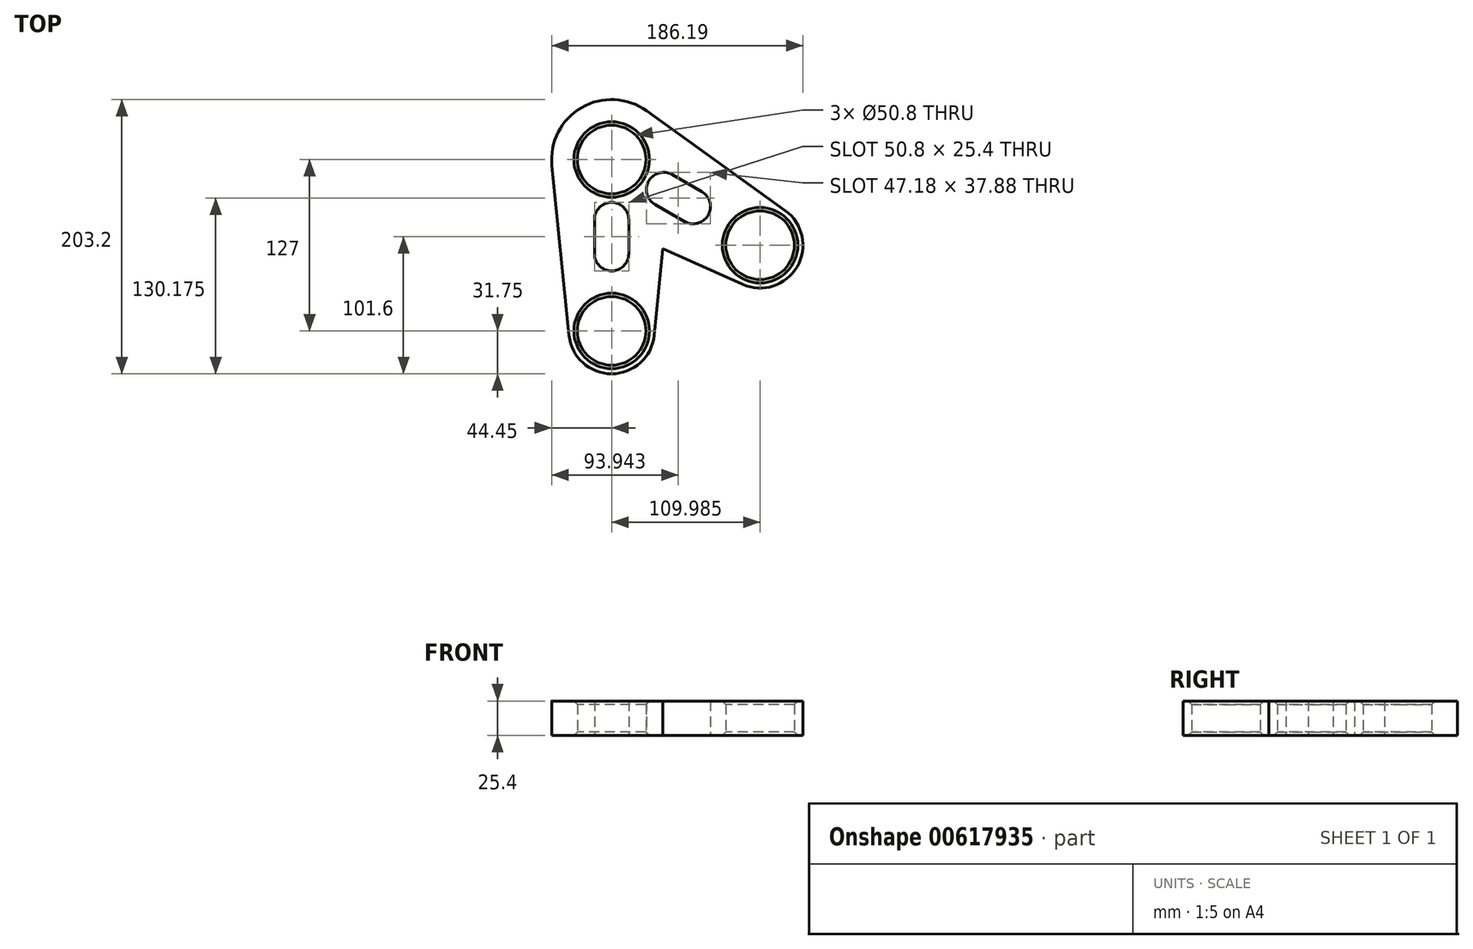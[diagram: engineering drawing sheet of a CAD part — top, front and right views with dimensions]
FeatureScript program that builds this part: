
annotation { "Feature Type Name" : "Feature", "Feature Type Description" : "" }
export const myFeature = defineFeature(function(context is Context, id is Id, definition is map)
    precondition{}
    {
        {
            var Q0;
            Q0=qCreatedBy(makeId("Top.planeOp"),FACE);
            var sketch = newSketch(context, id + "F0", { "sketchPlane" : qUnion([Q0])});
            skCircle(sketch, "E0", {"center": v(0, 0) * mm, "radius": 44.45 * mm});
            skCircle(sketch, "E1", {"center": v(0, -127) * mm, "radius": 31.75 * mm});
            skCircle(sketch, "E2", {"center": v(109.99, -63.5) * mm, "radius": 31.75 * mm});
            skLineSegment(sketch, "E3", {"start": v(0, 0) * mm, "end": v(0, -127) * mm});
            skLineSegment(sketch, "E4", {"start": v(0, 0) * mm, "end": v(109.99, -63.5) * mm});
            skLineSegment(sketch, "E5", {"start": v(-31.6, -130.18) * mm, "end": v(-44.23, -4.45) * mm});
            skLineSegment(sketch, "E6", {"start": v(96.94, -92.45) * mm, "end": v(-18.26, -40.52) * mm});
            skLineSegment(sketch, "E7", {"start": v(128.53, -37.73) * mm, "end": v(25.96, 36.08) * mm});
            skLineSegment(sketch, "E8", {"start": v(44.23, -4.44) * mm, "end": v(31.6, -130.18) * mm});
            skCircle(sketch, "E9", {"center": v(0, 0) * mm, "radius": 25.4 * mm});
            skCircle(sketch, "E10", {"center": v(0, -127) * mm, "radius": 25.4 * mm});
            skCircle(sketch, "E11", {"center": v(109.99, -63.5) * mm, "radius": 25.4 * mm});
            skSolve(sketch);
        }
        {
            var Q0;
            Q0=makeQuery(id+"F0.imprint","IMPRINT",FACE,{"disambiguationData":[TD([[makeQuery(id+"F0.imprint","IMPRINT",EDGE,{"derivedFrom":sQuery(id+"F0.wireOp",EDGE,"E10")}),-1.0]])]});
            var Q1;
            {var subQ0=sQuery(id+"F0.wireOp",EDGE,"E8");var subQ1=sQuery(id+"F0.wireOp",EDGE,"E1");var subQ2=makeQuery(id+"F0.imprint","INTERSECT",VERTEX,{"derivedFrom":[subQ1,subQ0]});Q1=makeQuery(id+"F0.imprint","IMPRINT",FACE,{"disambiguationData":[TD([[makeQuery(id+"F0.imprint","IMPRINT",EDGE,{"disambiguationData":[TD([[subQ2,-1.0]])],"derivedFrom":subQ1}),-1.0]])]});}
            var Q2;
            {var subQ0=sQuery(id+"F0.wireOp",EDGE,"E5");Q2=makeQuery(id+"F0.imprint","IMPRINT",FACE,{"disambiguationData":[TD([[makeQuery(id+"F0.imprint","IMPRINT",EDGE,{"derivedFrom":subQ0}),-1.0]])]});}
            var Q3;
            {var subQ3=sQuery(id+"F0.wireOp",EDGE,"E3");var subQ5=sQuery(id+"F0.wireOp",EDGE,"E0");var subQ6=makeQuery(id+"F0.imprint","INTERSECT",VERTEX,{"derivedFrom":[subQ5,subQ3]});Q3=makeQuery(id+"F0.imprint","IMPRINT",FACE,{"disambiguationData":[TD([[makeQuery(id+"F0.imprint","IMPRINT",EDGE,{"disambiguationData":[TD([[subQ6,-1.0]])],"derivedFrom":subQ5}),-1.0]])]});}
            var Q4;
            {var subQ0=sQuery(id+"F0.wireOp",EDGE,"E6");var subQ1=sQuery(id+"F0.wireOp",EDGE,"E0");var subQ2=makeQuery(id+"F0.imprint","INTERSECT",VERTEX,{"derivedFrom":[subQ1,subQ0]});Q4=makeQuery(id+"F0.imprint","IMPRINT",FACE,{"disambiguationData":[TD([[makeQuery(id+"F0.imprint","IMPRINT",EDGE,{"disambiguationData":[TD([[subQ2,-1.0]])],"derivedFrom":subQ1}),-1.0]])]});}
            var Q5;
            {var subQ0=sQuery(id+"F0.wireOp",EDGE,"E3");var subQ1=sQuery(id+"F0.wireOp",EDGE,"E0");var subQ2=makeQuery(id+"F0.imprint","INTERSECT",VERTEX,{"derivedFrom":[subQ1,subQ0]});Q5=makeQuery(id+"F0.imprint","IMPRINT",FACE,{"disambiguationData":[TD([[makeQuery(id+"F0.imprint","IMPRINT",EDGE,{"disambiguationData":[TD([[subQ2,-1.0]])],"derivedFrom":subQ1}),1.0]])]});}
            var Q6;
            {var subQ0=sQuery(id+"F0.wireOp",EDGE,"E0");var subQ9=makeQuery(id+"F0.imprint","INTERSECT",VERTEX,{"derivedFrom":[subQ0,sQuery(id+"F0.wireOp",EDGE,"E5")]});Q6=makeQuery(id+"F0.imprint","IMPRINT",FACE,{"disambiguationData":[TD([[makeQuery(id+"F0.imprint","IMPRINT",EDGE,{"disambiguationData":[TD([[subQ9,1.0]])],"derivedFrom":subQ0}),1.0]])]});}
            var Q7;
            {var subQ0=sQuery(id+"F0.wireOp",EDGE,"E8");var subQ1=sQuery(id+"F0.wireOp",EDGE,"E0");var subQ2=makeQuery(id+"F0.imprint","INTERSECT",VERTEX,{"derivedFrom":[subQ1,subQ0]});Q7=makeQuery(id+"F0.imprint","IMPRINT",FACE,{"disambiguationData":[TD([[makeQuery(id+"F0.imprint","IMPRINT",EDGE,{"disambiguationData":[TD([[subQ2,1.0]])],"derivedFrom":subQ1}),-1.0]])]});}
            var Q8;
            {var subQ0=sQuery(id+"F0.wireOp",EDGE,"E6");var subQ1=sQuery(id+"F0.wireOp",EDGE,"E2");var subQ2=makeQuery(id+"F0.imprint","INTERSECT",VERTEX,{"derivedFrom":[subQ1,subQ0]});Q8=makeQuery(id+"F0.imprint","IMPRINT",FACE,{"disambiguationData":[TD([[makeQuery(id+"F0.imprint","IMPRINT",EDGE,{"disambiguationData":[TD([[subQ2,1.0]])],"derivedFrom":subQ1}),-1.0]])]});}
            var Q9;
            {var subQ0=sQuery(id+"F0.wireOp",EDGE,"E7");Q9=makeQuery(id+"F0.imprint","IMPRINT",FACE,{"disambiguationData":[TD([[makeQuery(id+"F0.imprint","IMPRINT",EDGE,{"derivedFrom":subQ0}),1.0]])]});}
            var Q10;
            Q10=makeQuery(id+"F0.imprint","IMPRINT",FACE,{"disambiguationData":[TD([[makeQuery(id+"F0.imprint","IMPRINT",EDGE,{"derivedFrom":sQuery(id+"F0.wireOp",EDGE,"E11")}),-1.0]])]});
            extrude(context, id + "F1", {"entities" : qUnion([Q0, Q1, Q2, Q3, Q4, Q5, Q6, Q7, Q8, Q9, Q10]), "depth" : 25.4 * mm, "offsetDistance" : 25.4 * mm});
        }
        {
            var Q0;
            Q0=makeQuery(id+"F1.opExtrude","CAP_FACE",FACE,{"disambiguationData":[OSD([sQuery(id+"F0.wireOp",EDGE,"E0"),sQuery(id+"F0.wireOp",EDGE,"E1"),sQuery(id+"F0.wireOp",EDGE,"E2"),sQuery(id+"F0.wireOp",EDGE,"E5"),sQuery(id+"F0.wireOp",EDGE,"E6"),sQuery(id+"F0.wireOp",EDGE,"E7"),sQuery(id+"F0.wireOp",EDGE,"E8"),sQuery(id+"F0.wireOp",EDGE,"E9"),sQuery(id+"F0.wireOp",EDGE,"E10"),sQuery(id+"F0.wireOp",EDGE,"E11")])],"isStart":true});
            var sketch = newSketch(context, id + "F2", { "sketchPlane" : qUnion([Q0])});
            skLineSegment(sketch, "E12", {"start": v(0, 0) * mm, "end": v(0, 0) * mm});
            skArc(sketch, "E13.0.startCap", {"start": v(44.84, 11.23) * mm, "mid": v(27.5, 15.87) * mm, "end": v(32.14, 33.22) * mm});
            skArc(sketch, "E13.0.endCap", {"start": v(54.14, 45.92) * mm, "mid": v(71.5, 41.27) * mm, "end": v(66.84, 23.93) * mm});
            skLineSegment(sketch, "E13.0.left", {"start": v(32.14, 33.22) * mm, "end": v(54.14, 45.92) * mm});
            skLineSegment(sketch, "E13.0.right", {"start": v(44.84, 11.23) * mm, "end": v(66.84, 23.93) * mm});
            skLineSegment(sketch, "E14.MirrorCS", {"start": v(12.7, 44.45) * mm, "end": v(12.7, 69.85) * mm});
            skArc(sketch, "E15.MirrorCS", {"start": v(12.7, 69.85) * mm, "mid": v(0, 82.55) * mm, "end": v(-12.7, 69.85) * mm});
            skLineSegment(sketch, "E16.MirrorCS", {"start": v(-12.7, 44.45) * mm, "end": v(-12.7, 69.85) * mm});
            skArc(sketch, "E17.MirrorCS", {"start": v(-12.7, 44.45) * mm, "mid": v(0, 31.75) * mm, "end": v(12.7, 44.45) * mm});
            skSolve(sketch);
        }
        {
            var Q0;
            Q0 = qSketchRegion(id + "F2", true);
            extrude(context, id + "F3", {"entities" : qUnion([Q0]), "operationType" : NewBodyOperationType.REMOVE, "oppositeDirection" : true, "depth" : 25.4 * mm, "offsetDistance" : 25.4 * mm});
        }
        {
            var Q0;
            Q0=makeQuery(id+"F3.boolean.opBoolean","COPY",EDGE,{"derivedFrom":makeQuery(id+"F3.opExtrude","CAP_EDGE",EDGE,{"disambiguationData":[OSD([sQuery(id+"F2.wireOp",EDGE,"E13.0.left")])],"isStart":false})});
            var Q1;
            Q1=makeQuery(id+"F1.opExtrude","CAP_EDGE",EDGE,{"disambiguationData":[OSD([sQuery(id+"F0.wireOp",EDGE,"E11")])],"isStart":false});
            var Q2;
            Q2=makeQuery(id+"F3.boolean.opBoolean","COPY",EDGE,{"derivedFrom":makeQuery(id+"F3.opExtrude","CAP_EDGE",EDGE,{"disambiguationData":[OSD([sQuery(id+"F2.wireOp",EDGE,"E16.MirrorCS")])],"isStart":false})});
            var Q3;
            Q3=makeQuery(id+"F1.opExtrude","CAP_EDGE",EDGE,{"disambiguationData":[OSD([sQuery(id+"F0.wireOp",EDGE,"E10")])],"isStart":false});
            var Q4;
            Q4=makeQuery(id+"F1.opExtrude","CAP_EDGE",EDGE,{"disambiguationData":[OSD([sQuery(id+"F0.wireOp",EDGE,"E9")])],"isStart":false});
            var Q5;
            Q5=makeQuery(id+"F3.boolean.opBoolean","COPY",EDGE,{"derivedFrom":makeQuery(id+"F3.opExtrude","CAP_EDGE",EDGE,{"disambiguationData":[OSD([sQuery(id+"F2.wireOp",EDGE,"E13.0.startCap")])],"isStart":true})});
            var Q6;
            Q6=makeQuery(id+"F1.opExtrude","CAP_EDGE",EDGE,{"disambiguationData":[OSD([sQuery(id+"F0.wireOp",EDGE,"E11")])],"isStart":true});
            var Q7;
            Q7=makeQuery(id+"F1.opExtrude","CAP_EDGE",EDGE,{"disambiguationData":[OSD([sQuery(id+"F0.wireOp",EDGE,"E9")])],"isStart":true});
            var Q8;
            Q8=makeQuery(id+"F3.boolean.opBoolean","COPY",EDGE,{"derivedFrom":makeQuery(id+"F3.opExtrude","CAP_EDGE",EDGE,{"disambiguationData":[OSD([sQuery(id+"F2.wireOp",EDGE,"E14.MirrorCS")])],"isStart":true})});
            var Q9;
            Q9=makeQuery(id+"F1.opExtrude","CAP_EDGE",EDGE,{"disambiguationData":[OSD([sQuery(id+"F0.wireOp",EDGE,"E10")])],"isStart":true});
            chamfer(context, id + "F4", {"entities" : qUnion([Q0, Q1, Q2, Q3, Q4, Q5, Q6, Q7, Q8, Q9]), "width" : 2.54 * mm, "tangentPropagation" : true});
        }
    });
